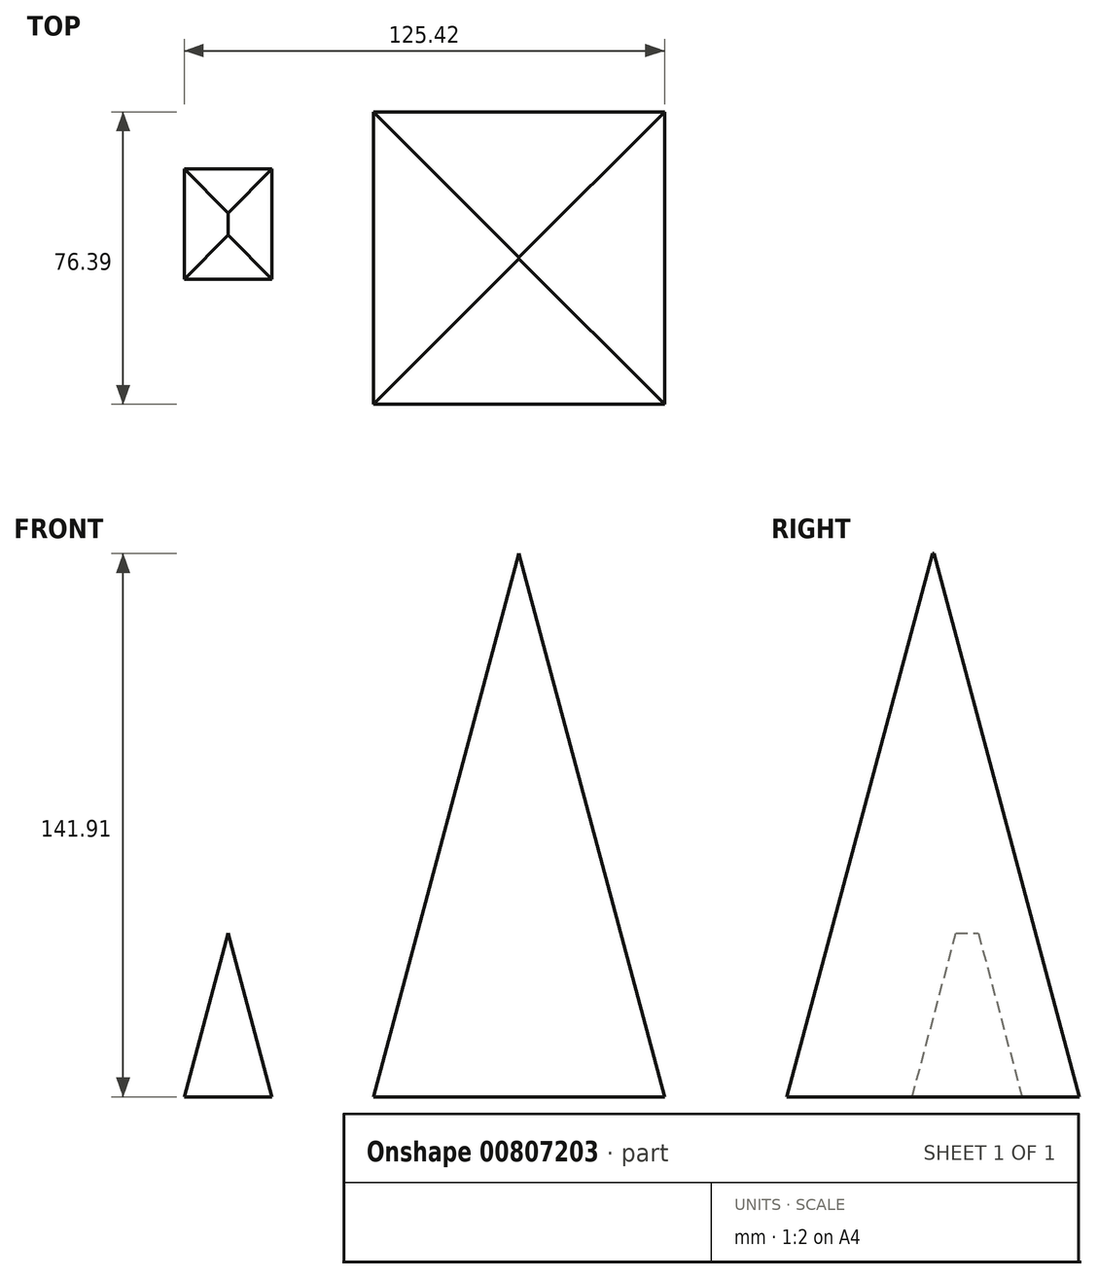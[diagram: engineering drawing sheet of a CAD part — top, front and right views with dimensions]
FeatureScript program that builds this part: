
annotation { "Feature Type Name" : "Feature", "Feature Type Description" : "" }
export const myFeature = defineFeature(function(context is Context, id is Id, definition is map)
    precondition{}
    {
        {
            var Q0;
            Q0=qCreatedBy(makeId("Top.planeOp"),FACE);
            var sketch = newSketch(context, id + "F0", { "sketchPlane" : qUnion([Q0])});
            skLineSegment(sketch, "E0.bottom", {"start": v(-34.59, -138.11) * mm, "end": v(-66.53, -138.11) * mm});
            skLineSegment(sketch, "E0.top", {"start": v(-34.59, -151.62) * mm, "end": v(-66.53, -151.62) * mm});
            skLineSegment(sketch, "E0.left", {"start": v(-34.59, -138.11) * mm, "end": v(-34.59, -151.62) * mm});
            skLineSegment(sketch, "E0.right", {"start": v(-66.53, -138.11) * mm, "end": v(-66.53, -151.62) * mm});
            skLineSegment(sketch, "E1.bottom", {"start": v(227.57, -135.7) * mm, "end": v(186.84, -135.7) * mm});
            skLineSegment(sketch, "E1.top", {"start": v(227.57, -116) * mm, "end": v(186.84, -116) * mm});
            skLineSegment(sketch, "E1.left", {"start": v(227.57, -135.7) * mm, "end": v(227.57, -116) * mm});
            skLineSegment(sketch, "E1.right", {"start": v(186.84, -135.7) * mm, "end": v(186.84, -116) * mm});
            skLineSegment(sketch, "E2.bottom", {"start": v(76.05, -76.4) * mm, "end": v(0, -76.4) * mm});
            skLineSegment(sketch, "E2.top", {"start": v(76.05, 0) * mm, "end": v(0, 0) * mm});
            skLineSegment(sketch, "E2.left", {"start": v(76.05, -76.4) * mm, "end": v(76.05, 0) * mm});
            skLineSegment(sketch, "E2.right", {"start": v(0, -76.4) * mm, "end": v(0, 0) * mm});
            skLineSegment(sketch, "E3.bottom", {"start": v(-49.37, -43.68) * mm, "end": v(-26.47, -43.68) * mm});
            skLineSegment(sketch, "E3.top", {"start": v(-49.37, -14.95) * mm, "end": v(-26.47, -14.95) * mm});
            skLineSegment(sketch, "E3.left", {"start": v(-49.37, -43.68) * mm, "end": v(-49.37, -14.95) * mm});
            skLineSegment(sketch, "E3.right", {"start": v(-26.47, -43.68) * mm, "end": v(-26.47, -14.95) * mm});
            skSolve(sketch);
        }
        {
            var Q0;
            Q0=makeQuery(id+"F0.imprint","IMPRINT",FACE,{"disambiguationData":[TD([[makeQuery(id+"F0.imprint","IMPRINT",EDGE,{"derivedFrom":sQuery(id+"F0.wireOp",EDGE,"E2.bottom")}),-1.0]])]});
            var Q1;
            Q1=makeQuery(id+"F0.imprint","IMPRINT",FACE,{"disambiguationData":[TD([[makeQuery(id+"F0.imprint","IMPRINT",EDGE,{"derivedFrom":sQuery(id+"F0.wireOp",EDGE,"E3.bottom")}),1.0]])]});
            extrude(context, id + "F1", {"entities" : qUnion([Q0, Q1]), "depth" : 304.8 * mm, "offsetDistance" : 25.4 * mm, "hasDraft" : true, "draftAngle" : 15 * degree, "draftPullDirection" : true});
        }
    });
